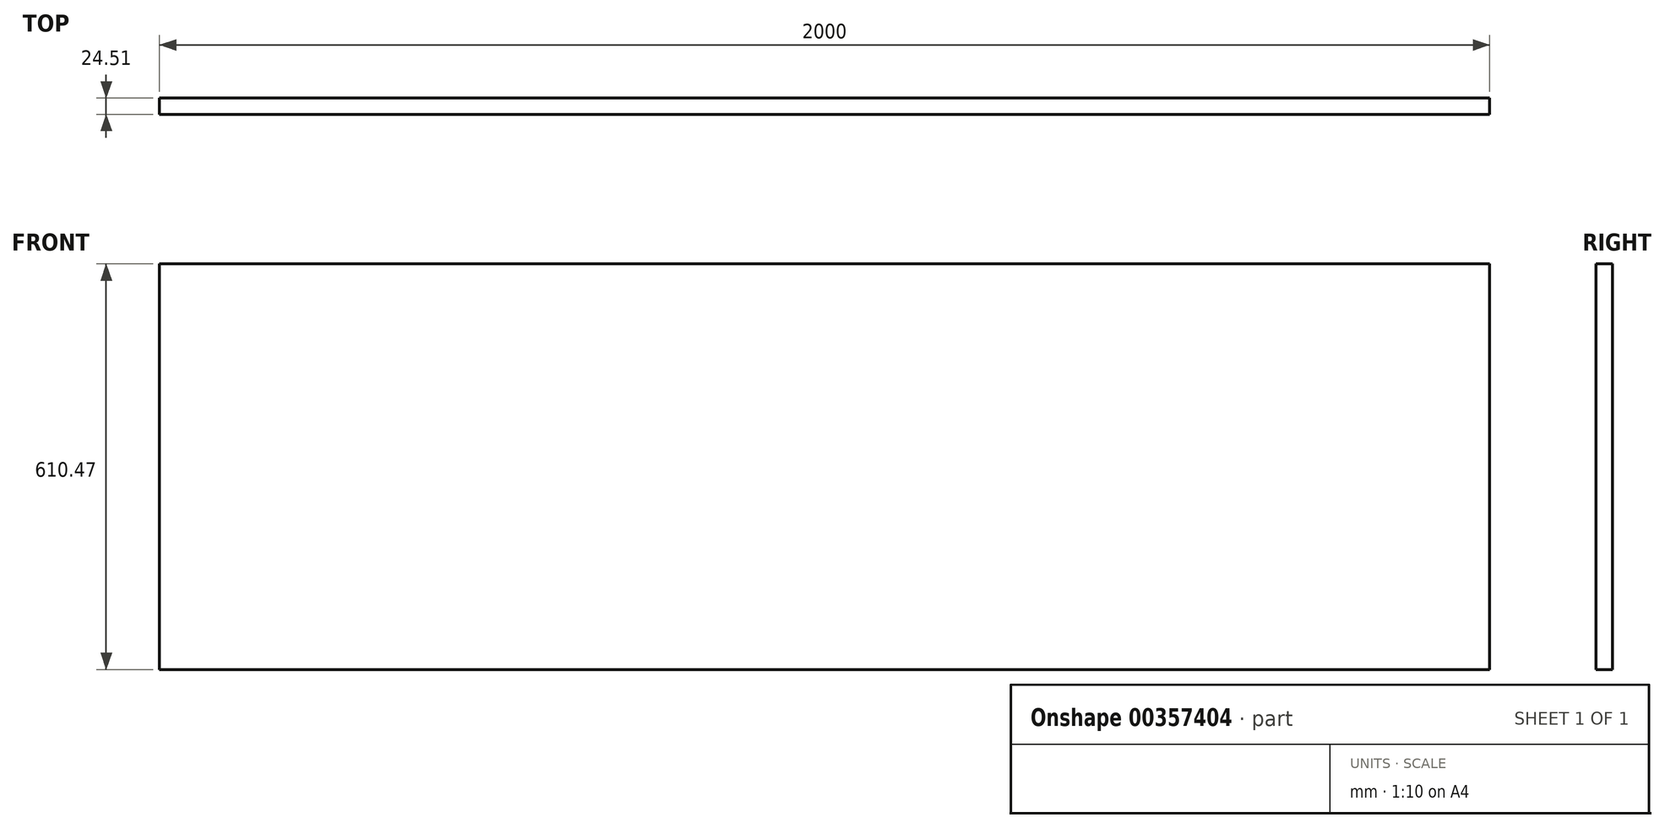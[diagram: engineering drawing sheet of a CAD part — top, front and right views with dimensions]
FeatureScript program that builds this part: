
annotation { "Feature Type Name" : "Feature", "Feature Type Description" : "" }
export const myFeature = defineFeature(function(context is Context, id is Id, definition is map)
    precondition{}
    {
        {
            var Q0;
            Q0=qCreatedBy(makeId("Right.planeOp"),FACE);
            var sketch = newSketch(context, id + "F0", { "sketchPlane" : qUnion([Q0])});
            skLineSegment(sketch, "E0.bottom", {"start": v(30.19, 283.4) * mm, "end": v(54.7, 283.4) * mm});
            skLineSegment(sketch, "E0.top", {"start": v(30.19, -327.07) * mm, "end": v(54.7, -327.07) * mm});
            skLineSegment(sketch, "E0.left", {"start": v(30.19, 283.4) * mm, "end": v(30.19, -327.07) * mm});
            skLineSegment(sketch, "E0.right", {"start": v(54.7, 283.4) * mm, "end": v(54.7, -327.07) * mm});
            skSolve(sketch);
        }
        {
            var Q0;
            Q0=makeQuery(id+"F0.imprint","IMPRINT",FACE,{"disambiguationData":[TD([[makeQuery(id+"F0.imprint","IMPRINT",EDGE,{"derivedFrom":sQuery(id+"F0.wireOp",EDGE,"E0.bottom")}),-1.0]])]});
            extrude(context, id + "F1", {"entities" : qUnion([Q0]), "depth" : 2000 * mm});
        }
    });
